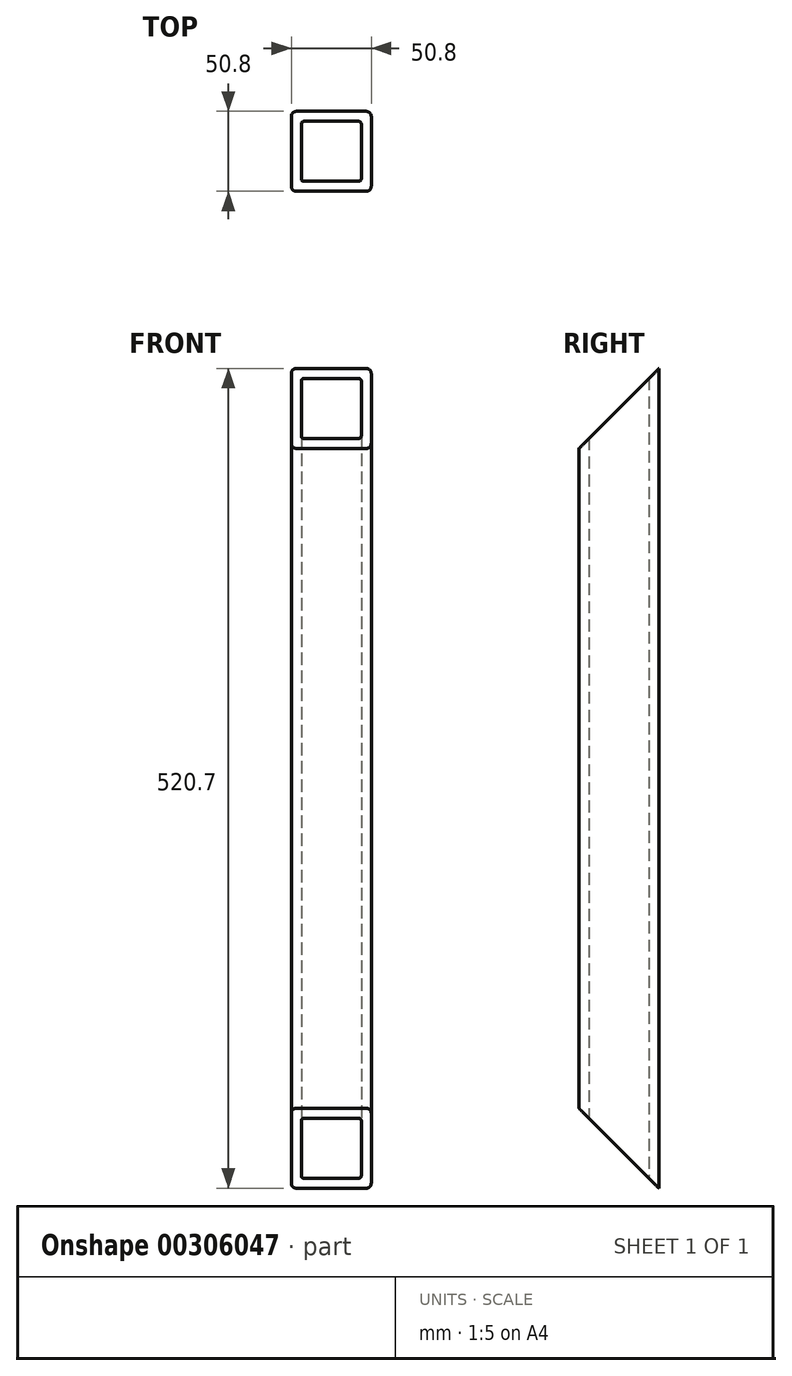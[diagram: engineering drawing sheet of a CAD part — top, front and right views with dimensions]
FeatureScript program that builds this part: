
annotation { "Feature Type Name" : "Feature", "Feature Type Description" : "" }
export const myFeature = defineFeature(function(context is Context, id is Id, definition is map)
    precondition{}
    {
        {
            var Q0;
            Q0=qCreatedBy(makeId("Top.planeOp"),FACE);
            var sketch = newSketch(context, id + "F0", { "sketchPlane" : qUnion([Q0])});
            skLineSegment(sketch, "E0.bottom", {"start": v(-22.22, 25.4) * mm, "end": v(22.23, 25.4) * mm});
            skLineSegment(sketch, "E0.top", {"start": v(-22.23, -25.4) * mm, "end": v(22.23, -25.4) * mm});
            skLineSegment(sketch, "E0.left", {"start": v(-25.4, 22.22) * mm, "end": v(-25.4, -22.23) * mm});
            skLineSegment(sketch, "E0.right", {"start": v(25.4, 22.22) * mm, "end": v(25.4, -22.23) * mm});
            skPoint(sketch, "E0.middle", {"position": v(0, 0) * mm});
            skPoint(sketch, "E1.visualSharp", {"position": v(-25.4, 25.4) * mm});
            skArc(sketch, "E1.filletArc", {"start": v(-22.22, 25.4) * mm, "mid": v(-24.47, 24.47) * mm, "end": v(-25.4, 22.22) * mm});
            skPoint(sketch, "E2.visualSharp", {"position": v(-25.4, -25.4) * mm});
            skArc(sketch, "E2.filletArc", {"start": v(-25.4, -22.23) * mm, "mid": v(-24.47, -24.47) * mm, "end": v(-22.23, -25.4) * mm});
            skPoint(sketch, "E3.visualSharp", {"position": v(25.4, -25.4) * mm});
            skArc(sketch, "E3.filletArc", {"start": v(22.23, -25.4) * mm, "mid": v(24.47, -24.47) * mm, "end": v(25.4, -22.23) * mm});
            skPoint(sketch, "E4.visualSharp", {"position": v(25.4, 25.4) * mm});
            skArc(sketch, "E4.filletArc", {"start": v(25.4, 22.22) * mm, "mid": v(24.47, 24.47) * mm, "end": v(22.23, 25.4) * mm});
            skLineSegment(sketch, "E5.0", {"start": v(-17.46, 19.05) * mm, "end": v(17.46, 19.05) * mm});
            skLineSegment(sketch, "E5.1", {"start": v(-19.05, 17.46) * mm, "end": v(-19.05, -17.46) * mm});
            skLineSegment(sketch, "E5.2", {"start": v(-17.46, -19.05) * mm, "end": v(17.46, -19.05) * mm});
            skLineSegment(sketch, "E5.3", {"start": v(19.05, 17.46) * mm, "end": v(19.05, -17.46) * mm});
            skPoint(sketch, "E6.visualSharp", {"position": v(-19.05, 19.05) * mm});
            skArc(sketch, "E6.filletArc", {"start": v(-17.46, 19.05) * mm, "mid": v(-18.59, 18.59) * mm, "end": v(-19.05, 17.46) * mm});
            skPoint(sketch, "E7.visualSharp", {"position": v(-19.05, -19.05) * mm});
            skArc(sketch, "E7.filletArc", {"start": v(-19.05, -17.46) * mm, "mid": v(-18.59, -18.59) * mm, "end": v(-17.46, -19.05) * mm});
            skPoint(sketch, "E8.visualSharp", {"position": v(19.05, -19.05) * mm});
            skArc(sketch, "E8.filletArc", {"start": v(17.46, -19.05) * mm, "mid": v(18.59, -18.59) * mm, "end": v(19.05, -17.46) * mm});
            skPoint(sketch, "E9.visualSharp", {"position": v(19.05, 19.05) * mm});
            skArc(sketch, "E9.filletArc", {"start": v(19.05, 17.46) * mm, "mid": v(18.59, 18.59) * mm, "end": v(17.46, 19.05) * mm});
            skSolve(sketch);
        }
        {
            var Q0;
            Q0=makeQuery(id+"F0.imprint","IMPRINT",FACE,{"disambiguationData":[TD([[makeQuery(id+"F0.imprint","IMPRINT",EDGE,{"derivedFrom":sQuery(id+"F0.wireOp",EDGE,"E0.bottom")}),-1.0]])]});
            extrude(context, id + "F1", {"entities" : qUnion([Q0]), "endBound" : BoundingType.SYMMETRIC, "depth" : 520.7 * mm});
        }
        {
            var Q0;
            Q0=makeQuery(id+"F1.opExtrude","SWEPT_FACE",FACE,{"disambiguationData":[OSD([sQuery(id+"F0.wireOp",EDGE,"E0.right")])]});
            var sketch = newSketch(context, id + "F2", { "sketchPlane" : qUnion([Q0])});
            skLineSegment(sketch, "E10", {"start": v(25.4, 260.35) * mm, "end": v(-25.4, 209.55) * mm});
            skLineSegment(sketch, "E11", {"start": v(-25.4, 209.55) * mm, "end": v(-25.4, 260.35) * mm});
            skLineSegment(sketch, "E12", {"start": v(-25.4, 260.35) * mm, "end": v(25.4, 260.35) * mm});
            skLineSegment(sketch, "E13", {"start": v(25.4, -260.35) * mm, "end": v(-25.4, -209.55) * mm});
            skLineSegment(sketch, "E14", {"start": v(-25.4, -209.55) * mm, "end": v(-25.4, -260.35) * mm});
            skLineSegment(sketch, "E15", {"start": v(-25.4, -260.35) * mm, "end": v(25.4, -260.35) * mm});
            skSolve(sketch);
        }
        {
            var Q0;
            Q0=qSketchRegion(id+"F2",true);
            extrude(context, id + "F3", {"entities" : qUnion([Q0]), "operationType" : NewBodyOperationType.REMOVE, "endBound" : BoundingType.THROUGH_ALL, "oppositeDirection" : true, "depth" : 25.4 * mm});
        }
    });
